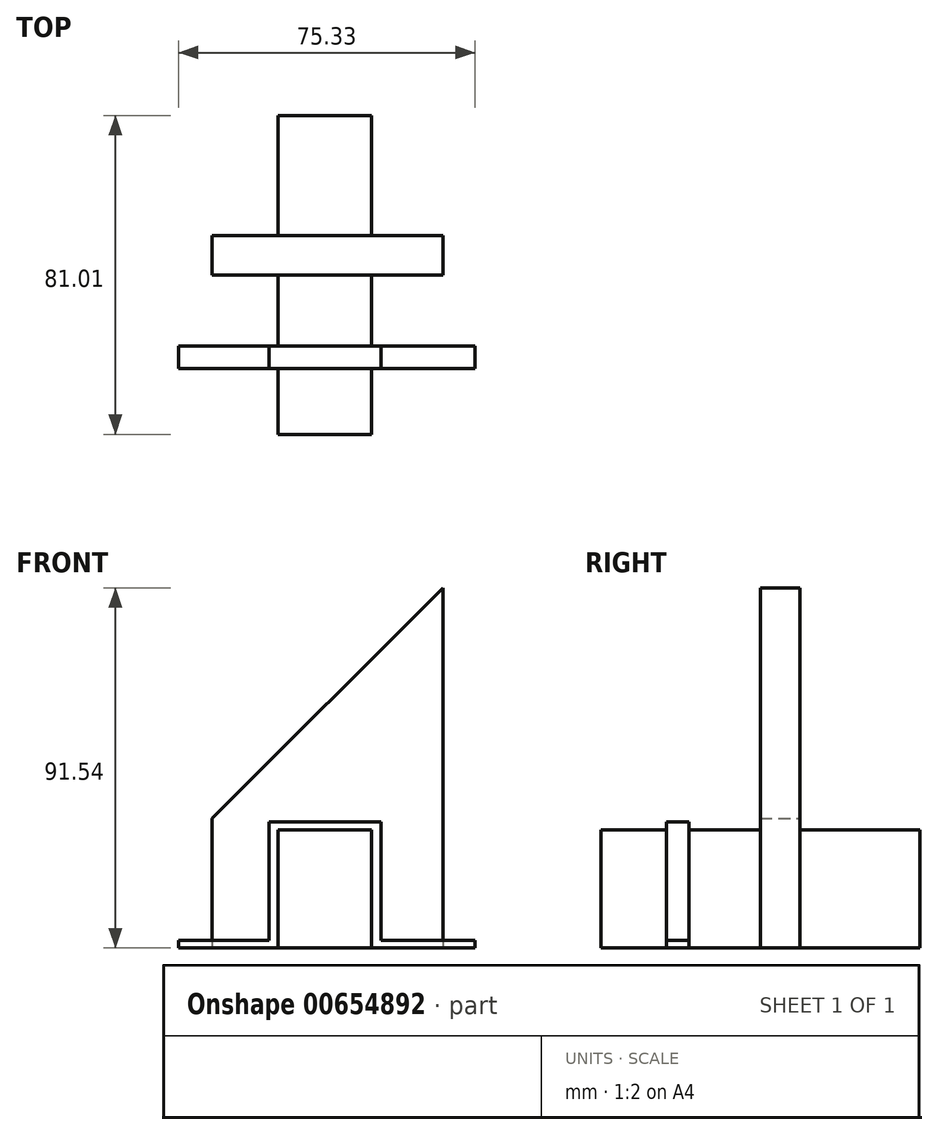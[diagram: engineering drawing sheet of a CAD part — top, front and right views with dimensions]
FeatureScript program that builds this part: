
annotation { "Feature Type Name" : "Feature", "Feature Type Description" : "" }
export const myFeature = defineFeature(function(context is Context, id is Id, definition is map)
    precondition{}
    {
        {
            var Q0;
            Q0=qCreatedBy(makeId("Top.planeOp"),FACE);
            var sketch = newSketch(context, id + "F0", { "sketchPlane" : qUnion([Q0])});
            skLineSegment(sketch, "E0.bottom", {"start": v(-12.27, 24.9) * mm, "end": v(11.56, 24.9) * mm});
            skLineSegment(sketch, "E0.top", {"start": v(-12.27, -56.1) * mm, "end": v(11.56, -56.1) * mm});
            skLineSegment(sketch, "E0.left", {"start": v(-12.27, 24.9) * mm, "end": v(-12.27, -56.1) * mm});
            skLineSegment(sketch, "E0.right", {"start": v(11.56, 24.9) * mm, "end": v(11.56, -56.1) * mm});
            skPoint(sketch, "E1.oppositeSnap0", {"position": v(11.56, -15.6) * mm});
            skLineSegment(sketch, "E1.bottom", {"start": v(-28.95, -5.6) * mm, "end": v(29.66, -5.6) * mm});
            skLineSegment(sketch, "E1.top", {"start": v(-28.95, -15.6) * mm, "end": v(29.66, -15.6) * mm});
            skLineSegment(sketch, "E1.left", {"start": v(-28.95, -5.6) * mm, "end": v(-28.95, -15.6) * mm});
            skLineSegment(sketch, "E1.right", {"start": v(29.66, -5.6) * mm, "end": v(29.66, -15.6) * mm});
            skLineSegment(sketch, "E2", {"start": v(-61.88, 62.91) * mm, "end": v(-61.88, -91.69) * mm});
            skLineSegment(sketch, "E3.bottom", {"start": v(-37.55, -33.7) * mm, "end": v(37.78, -33.7) * mm});
            skLineSegment(sketch, "E3.top", {"start": v(-37.55, -39.4) * mm, "end": v(37.78, -39.4) * mm});
            skLineSegment(sketch, "E3.left", {"start": v(-37.55, -33.7) * mm, "end": v(-37.55, -39.4) * mm});
            skLineSegment(sketch, "E3.right", {"start": v(37.78, -33.7) * mm, "end": v(37.78, -39.4) * mm});
            skSolve(sketch);
        }
        {
            var Q0;
            {var subQ0=sQuery(id+"F0.wireOp",EDGE,"E0.top");Q0=makeQuery(id+"F0.imprint","IMPRINT",FACE,{"disambiguationData":[TD([[makeQuery(id+"F0.imprint","IMPRINT",EDGE,{"derivedFrom":subQ0}),1.0]])]});}
            var Q1;
            {var subQ0=sQuery(id+"F0.wireOp",EDGE,"E1.bottom");var subQ1=sQuery(id+"F0.wireOp",EDGE,"E0.left");var subQ2=makeQuery(id+"F0.imprint","INTERSECT",VERTEX,{"derivedFrom":[subQ1,subQ0]});Q1=makeQuery(id+"F0.imprint","IMPRINT",FACE,{"disambiguationData":[TD([[makeQuery(id+"F0.imprint","IMPRINT",EDGE,{"disambiguationData":[TD([[subQ2,-1.0]])],"derivedFrom":subQ1}),1.0]])]});}
            var Q2;
            {var subQ0=sQuery(id+"F0.wireOp",EDGE,"E0.bottom");Q2=makeQuery(id+"F0.imprint","IMPRINT",FACE,{"disambiguationData":[TD([[makeQuery(id+"F0.imprint","IMPRINT",EDGE,{"derivedFrom":subQ0}),-1.0]])]});}
            var Q3;
            {var subQ0=sQuery(id+"F0.wireOp",EDGE,"E1.top");var subQ1=sQuery(id+"F0.wireOp",EDGE,"E0.left");var subQ2=makeQuery(id+"F0.imprint","INTERSECT",VERTEX,{"derivedFrom":[subQ1,subQ0]});Q3=makeQuery(id+"F0.imprint","IMPRINT",FACE,{"disambiguationData":[TD([[makeQuery(id+"F0.imprint","IMPRINT",EDGE,{"disambiguationData":[TD([[subQ2,-1.0]])],"derivedFrom":subQ1}),1.0]])]});}
            var Q4;
            {var subQ0=sQuery(id+"F0.wireOp",EDGE,"E3.bottom");var subQ1=sQuery(id+"F0.wireOp",EDGE,"E0.left");var subQ2=makeQuery(id+"F0.imprint","INTERSECT",VERTEX,{"derivedFrom":[subQ1,subQ0]});Q4=makeQuery(id+"F0.imprint","IMPRINT",FACE,{"disambiguationData":[TD([[makeQuery(id+"F0.imprint","IMPRINT",EDGE,{"disambiguationData":[TD([[subQ2,-1.0]])],"derivedFrom":subQ1}),1.0]])]});}
            extrude(context, id + "F1", {"entities" : qUnion([Q0, Q1, Q2, Q3, Q4]), "depth" : 30 * mm, "offsetDistance" : 25 * mm});
        }
        {
            var Q0;
            Q0=sQuery(id+"F0.wireOp",EDGE,"E2");
            cPlane(context, id + "F2", {"entities" : qUnion([Q0]), "cplaneType" : CPlaneType.LINE_ANGLE, "offset" : 25 * mm, "angle" : 45 * degree, "width" : 150 * mm, "height" : 150 * mm});
        }
        {
            var Q0;
            {var subQ5=sQuery(id+"F0.wireOp",EDGE,"E1.left");Q0=makeQuery(id+"F0.imprint","IMPRINT",FACE,{"disambiguationData":[TD([[makeQuery(id+"F0.imprint","IMPRINT",EDGE,{"derivedFrom":subQ5}),1.0]])]});}
            var Q1;
            {var subQ5=sQuery(id+"F0.wireOp",EDGE,"E1.right");Q1=makeQuery(id+"F0.imprint","IMPRINT",FACE,{"disambiguationData":[TD([[makeQuery(id+"F0.imprint","IMPRINT",EDGE,{"derivedFrom":subQ5}),-1.0]])]});}
            var Q2;
            Q2=qCreatedBy(id+"F2.planeOp",FACE);
            extrude(context, id + "F3", {"entities" : qUnion([Q0, Q1]), "operationType" : NewBodyOperationType.ADD, "endBound" : BoundingType.UP_TO_SURFACE, "depth" : 100 * mm, "endBoundEntityFace" : qUnion([Q2]), "offsetDistance" : 25 * mm});
        }
        {
            var Q0;
            Q0=makeQuery(id+"F3.opExtrude","SWEPT_FACE",FACE,{"disambiguationData":[OSD([sQuery(id+"F0.wireOp",EDGE,"E0.left")])]});
            var Q1;
            Q1=makeQuery(id+"F3.opExtrude","SWEPT_FACE",FACE,{"disambiguationData":[OSD([sQuery(id+"F0.wireOp",EDGE,"E0.right")])]});
            var Q2;
            Q2=makeQuery(id+"F1.opExtrude","SWEPT_BODY",BODY,{"disambiguationData":[OSD([sQuery(id+"F0.wireOp",EDGE,"E0.bottom"),sQuery(id+"F0.wireOp",EDGE,"E0.top"),sQuery(id+"F0.wireOp",EDGE,"E0.left"),sQuery(id+"F0.wireOp",EDGE,"E0.right")])]});
            extrude(context, id + "F4", {"entities" : qUnion([Q0]), "operationType" : NewBodyOperationType.ADD, "endBound" : BoundingType.UP_TO_SURFACE, "depth" : 25 * mm, "endBoundEntityFace" : qUnion([Q1]), "endBoundEntityBody" : qUnion([Q2]), "offsetDistance" : 25 * mm});
        }
        {
            var Q0;
            Q0=makeQuery(id+"F4.opExtrude","SWEPT_FACE",FACE,{"disambiguationData":[OSD([sQuery(id+"F0.wireOp",EDGE,"E0.left"),dummyQuery(id+"F2.planeOp",FACE)])]});
            var Q1;
            Q1=qCreatedBy(id+"F2.planeOp",FACE);
            extrude(context, id + "F5", {"entities" : qUnion([Q0]), "operationType" : NewBodyOperationType.ADD, "endBound" : BoundingType.UP_TO_SURFACE, "depth" : 25 * mm, "endBoundEntityFace" : qUnion([Q1]), "offsetDistance" : 25 * mm});
        }
        {
            var Q0;
            {var subQ5=sQuery(id+"F0.wireOp",EDGE,"E3.right");Q0=makeQuery(id+"F0.imprint","IMPRINT",FACE,{"disambiguationData":[TD([[makeQuery(id+"F0.imprint","IMPRINT",EDGE,{"derivedFrom":subQ5}),-1.0]])]});}
            var Q1;
            {var subQ5=sQuery(id+"F0.wireOp",EDGE,"E3.left");Q1=makeQuery(id+"F0.imprint","IMPRINT",FACE,{"disambiguationData":[TD([[makeQuery(id+"F0.imprint","IMPRINT",EDGE,{"derivedFrom":subQ5}),1.0]])]});}
            extrude(context, id + "F6", {"entities" : qUnion([Q0, Q1]), "depth" : 2 * mm, "offsetDistance" : 25 * mm});
        }
        {
            var Q0;
            Q0=makeQuery(id+"F6.opExtrude","CAP_FACE",FACE,{"disambiguationData":[OSD([sQuery(id+"F0.wireOp",EDGE,"E0.left"),sQuery(id+"F0.wireOp",EDGE,"E3.bottom"),sQuery(id+"F0.wireOp",EDGE,"E3.top"),sQuery(id+"F0.wireOp",EDGE,"E3.left")])],"isStart":false});
            var sketch = newSketch(context, id + "F7", { "sketchPlane" : qUnion([Q0])});
            skLineSegment(sketch, "E4.bottom", {"start": v(-14.5, -33.7) * mm, "end": v(-12.27, -33.7) * mm});
            skLineSegment(sketch, "E4.top", {"start": v(-14.5, -39.4) * mm, "end": v(-12.27, -39.4) * mm});
            skLineSegment(sketch, "E4.left", {"start": v(-14.5, -33.7) * mm, "end": v(-14.5, -39.4) * mm});
            skLineSegment(sketch, "E4.right", {"start": v(-12.27, -33.7) * mm, "end": v(-12.27, -39.4) * mm});
            skLineSegment(sketch, "E5.bottom", {"start": v(11.56, -33.7) * mm, "end": v(13.87, -33.7) * mm});
            skLineSegment(sketch, "E5.top", {"start": v(11.56, -39.4) * mm, "end": v(13.87, -39.4) * mm});
            skLineSegment(sketch, "E5.left", {"start": v(11.56, -33.7) * mm, "end": v(11.56, -39.4) * mm});
            skLineSegment(sketch, "E5.right", {"start": v(13.87, -33.7) * mm, "end": v(13.87, -39.4) * mm});
            skSolve(sketch);
        }
        {
            var Q0;
            Q0=makeQuery(id+"F7.imprint","IMPRINT",FACE,{"disambiguationData":[TD([[makeQuery(id+"F7.imprint","IMPRINT",EDGE,{"derivedFrom":sQuery(id+"F7.wireOp",EDGE,"E5.bottom")}),-1.0]])]});
            var Q1;
            Q1=makeQuery(id+"F7.imprint","IMPRINT",FACE,{"disambiguationData":[TD([[makeQuery(id+"F7.imprint","IMPRINT",EDGE,{"derivedFrom":sQuery(id+"F7.wireOp",EDGE,"E4.bottom")}),-1.0]])]});
            extrude(context, id + "F8", {"entities" : qUnion([Q0, Q1]), "operationType" : NewBodyOperationType.ADD, "depth" : 30 * mm, "offsetDistance" : 25 * mm});
        }
        {
            var Q0;
            Q0=makeQuery(id+"F8.boolean.opBoolean","MERGE",FACE,{"derivedFrom":[makeQuery(id+"F6.opExtrude","SWEPT_FACE",FACE,{"disambiguationData":[OSD([sQuery(id+"F0.wireOp",EDGE,"E0.right")])]}),makeQuery(id+"F8.opExtrude","SWEPT_FACE",FACE,{"disambiguationData":[OSD([sQuery(id+"F7.wireOp",EDGE,"E5.left")])]})]});
            extrude(context, id + "F9", {"entities" : qUnion([Q0]), "operationType" : NewBodyOperationType.ADD, "depth" : 25 * mm, "offsetDistance" : 25 * mm});
        }
    });
